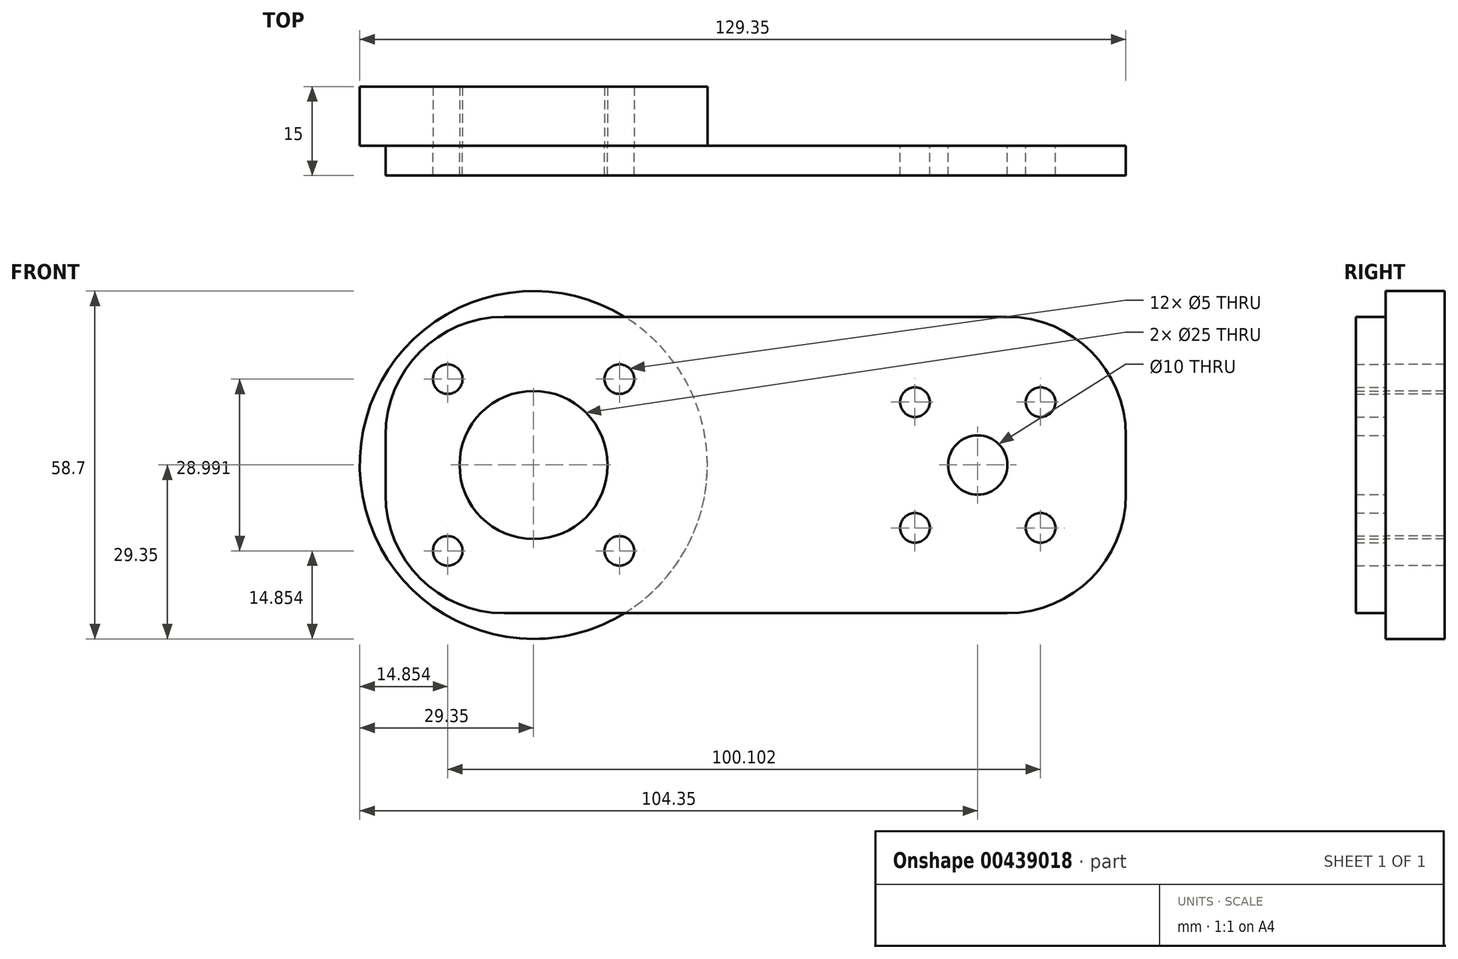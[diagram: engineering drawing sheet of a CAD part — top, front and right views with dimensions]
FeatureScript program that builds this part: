
annotation { "Feature Type Name" : "Feature", "Feature Type Description" : "" }
export const myFeature = defineFeature(function(context is Context, id is Id, definition is map)
    precondition{}
    {
        {
            var Q0;
            Q0=qCreatedBy(makeId("Front.planeOp"),FACE);
            var sketch = newSketch(context, id + "F0", { "sketchPlane" : qUnion([Q0])});
            skCircle(sketch, "E0", {"center": v(26.9, 10.6) * mm, "radius": 2.5 * mm});
            skCircle(sketch, "E1", {"center": v(26.9, -10.6) * mm, "radius": 2.5 * mm});
            skCircle(sketch, "E2", {"center": v(48.1, 10.6) * mm, "radius": 2.5 * mm});
            skCircle(sketch, "E3", {"center": v(48.1, -10.6) * mm, "radius": 2.5 * mm});
            skCircle(sketch, "E4", {"center": v(37.5, 0) * mm, "radius": 5 * mm});
            skLineSegment(sketch, "E5", {"start": v(26.9, 10.6) * mm, "end": v(37.5, 0) * mm});
            skLineSegment(sketch, "E6", {"start": v(48.1, 10.6) * mm, "end": v(37.5, 0) * mm});
            skCircle(sketch, "E7", {"center": v(-52, 14.5) * mm, "radius": 2.5 * mm});
            skCircle(sketch, "E8", {"center": v(-52, -14.5) * mm, "radius": 2.5 * mm});
            skCircle(sketch, "E9", {"center": v(-23, 14.5) * mm, "radius": 2.5 * mm});
            skCircle(sketch, "E10", {"center": v(-23, -14.5) * mm, "radius": 2.5 * mm});
            skCircle(sketch, "E11", {"center": v(-37.5, 0) * mm, "radius": 12.5 * mm});
            skLineSegment(sketch, "E12", {"start": v(-52, 14.5) * mm, "end": v(-37.5, 0) * mm});
            skLineSegment(sketch, "E13", {"start": v(-23, 14.5) * mm, "end": v(-37.5, 0) * mm});
            skLineSegment(sketch, "E14.bottom", {"start": v(42.5, 25) * mm, "end": v(-42.5, 25) * mm});
            skLineSegment(sketch, "E14.top", {"start": v(42.5, -25) * mm, "end": v(-42.5, -25) * mm});
            skLineSegment(sketch, "E14.left", {"start": v(62.5, 5) * mm, "end": v(62.5, -5) * mm});
            skLineSegment(sketch, "E14.right", {"start": v(-62.5, 5) * mm, "end": v(-62.5, -5) * mm});
            skPoint(sketch, "E14.middle", {"position": v(0, 0) * mm});
            skPoint(sketch, "E15.visualSharp", {"position": v(62.5, 25) * mm});
            skArc(sketch, "E15.filletArc", {"start": v(62.5, 5) * mm, "mid": v(56.64, 19.14) * mm, "end": v(42.5, 25) * mm});
            skPoint(sketch, "E16.visualSharp", {"position": v(62.5, -25) * mm});
            skArc(sketch, "E16.filletArc", {"start": v(42.5, -25) * mm, "mid": v(56.64, -19.14) * mm, "end": v(62.5, -5) * mm});
            skPoint(sketch, "E17.visualSharp", {"position": v(-62.5, 25) * mm});
            skArc(sketch, "E17.filletArc", {"start": v(-42.5, 25) * mm, "mid": v(-56.64, 19.14) * mm, "end": v(-62.5, 5) * mm});
            skPoint(sketch, "E18.visualSharp", {"position": v(-62.5, -25) * mm});
            skArc(sketch, "E18.filletArc", {"start": v(-62.5, -5) * mm, "mid": v(-56.64, -19.14) * mm, "end": v(-42.5, -25) * mm});
            skSolve(sketch);
        }
        {
            var Q0;
            Q0=makeQuery(id+"F0.imprint","IMPRINT",FACE,{"disambiguationData":[TD([[makeQuery(id+"F0.imprint","IMPRINT",EDGE,{"derivedFrom":sQuery(id+"F0.wireOp",EDGE,"E0")}),-1.0]])]});
            extrude(context, id + "F1", {"entities" : qUnion([Q0]), "depth" : 5 * mm});
        }
        {
            var Q0;
            Q0=qCreatedBy(makeId("Front.planeOp"),FACE);
            var sketch = newSketch(context, id + "F2", { "sketchPlane" : qUnion([Q0])});
            skCircle(sketch, "E19", {"center": v(-37.5, 0) * mm, "radius": 29.35 * mm});
            skCircle(sketch, "E20", {"center": v(-52, 14.5) * mm, "radius": 2.5 * mm});
            skCircle(sketch, "E21", {"center": v(-52, -14.5) * mm, "radius": 2.5 * mm});
            skCircle(sketch, "E22", {"center": v(-23, 14.5) * mm, "radius": 2.5 * mm});
            skCircle(sketch, "E23", {"center": v(-23, -14.5) * mm, "radius": 2.5 * mm});
            skCircle(sketch, "E24", {"center": v(-37.5, 0) * mm, "radius": 12.5 * mm});
            skLineSegment(sketch, "E25", {"start": v(-52, 14.5) * mm, "end": v(-37.5, 0) * mm});
            skLineSegment(sketch, "E26", {"start": v(-37.5, 0) * mm, "end": v(-23, 14.5) * mm});
            skLineSegment(sketch, "E27", {"start": v(-37.5, 0) * mm, "end": v(-23, -14.5) * mm});
            skLineSegment(sketch, "E28", {"start": v(-37.5, 0) * mm, "end": v(-52, -14.5) * mm});
            skSolve(sketch);
        }
        {
            var Q0;
            Q0 = qSketchRegion(id + "F2", true);
            extrude(context, id + "F3", {"entities" : qUnion([Q0]), "oppositeDirection" : true, "depth" : 10 * mm});
        }
    });
